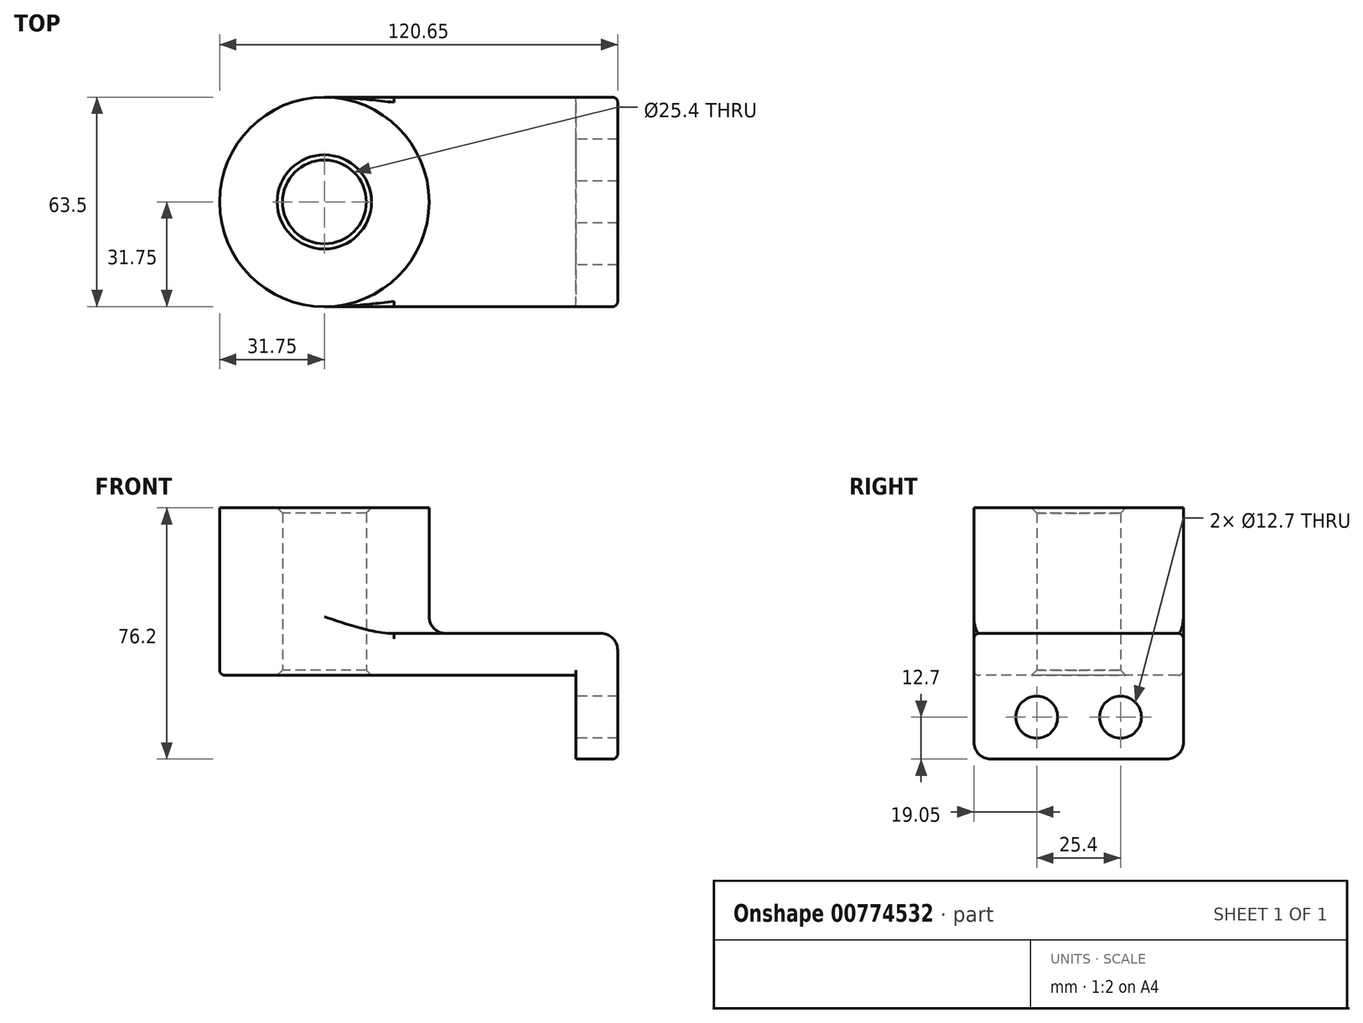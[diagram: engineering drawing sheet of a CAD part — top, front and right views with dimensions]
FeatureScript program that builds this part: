
annotation { "Feature Type Name" : "Feature", "Feature Type Description" : "" }
export const myFeature = defineFeature(function(context is Context, id is Id, definition is map)
    precondition{}
    {
        {
            var Q0;
            Q0=qCreatedBy(makeId("Top.planeOp"),FACE);
            var sketch = newSketch(context, id + "F0", { "sketchPlane" : qUnion([Q0])});
            skLineSegment(sketch, "E0.bottom", {"start": v(-38.1, 31.75) * mm, "end": v(38.1, 31.75) * mm});
            skLineSegment(sketch, "E0.top", {"start": v(-38.1, -31.75) * mm, "end": v(38.1, -31.75) * mm});
            skLineSegment(sketch, "E0.left", {"start": v(-38.1, 31.75) * mm, "end": v(-38.1, -31.75) * mm});
            skLineSegment(sketch, "E0.right", {"start": v(38.1, 31.75) * mm, "end": v(38.1, -31.75) * mm});
            skPoint(sketch, "E0.middle", {"position": v(0, 0) * mm});
            skCircle(sketch, "E1", {"center": v(-38.1, 0) * mm, "radius": 31.75 * mm});
            skCircle(sketch, "E2", {"center": v(-38.1, 0) * mm, "radius": 12.7 * mm});
            skSolve(sketch);
        }
        {
            var Q0;
            Q0 = qSketchRegion(id + "F0", true);
            extrude(context, id + "F1", {"entities" : qUnion([Q0]), "depth" : 12.7 * mm, "offsetDistance" : 25.4 * mm});
        }
        {
            var Q0;
            {var subQ1=sQuery(id+"F0.wireOp",EDGE,"E0.left");var subQ3=sQuery(id+"F0.wireOp",EDGE,"E2");var subQ4=makeQuery(id+"F0.imprint","INTERSECT",VERTEX,{"disambiguationData":[OD(0.0)],"derivedFrom":[subQ1,subQ3]});Q0=makeQuery(id+"F0.imprint","IMPRINT",FACE,{"disambiguationData":[TD([[makeQuery(id+"F0.imprint","IMPRINT",EDGE,{"disambiguationData":[TD([[subQ4,-1.0]])],"derivedFrom":subQ3}),-1.0]])]});}
            var Q1;
            {var subQ1=sQuery(id+"F0.wireOp",EDGE,"E0.left");var subQ3=sQuery(id+"F0.wireOp",EDGE,"E2");var subQ4=makeQuery(id+"F0.imprint","INTERSECT",VERTEX,{"disambiguationData":[OD(0.0)],"derivedFrom":[subQ1,subQ3]});Q1=makeQuery(id+"F0.imprint","IMPRINT",FACE,{"disambiguationData":[TD([[makeQuery(id+"F0.imprint","IMPRINT",EDGE,{"disambiguationData":[TD([[subQ4,1.0]])],"derivedFrom":subQ3}),-1.0]])]});}
            extrude(context, id + "F2", {"entities" : qUnion([Q0, Q1]), "operationType" : NewBodyOperationType.ADD, "depth" : 50.8 * mm, "offsetDistance" : 25.4 * mm});
        }
        {
            var Q0;
            Q0=makeQuery(id+"F1.opExtrude","SWEPT_FACE",FACE,{"disambiguationData":[OSD([sQuery(id+"F0.wireOp",EDGE,"E0.right")])]});
            var sketch = newSketch(context, id + "F3", { "sketchPlane" : qUnion([Q0])});
            skLineSegment(sketch, "E3.bottom", {"start": v(-31.75, 12.7) * mm, "end": v(31.75, 12.7) * mm});
            skLineSegment(sketch, "E3.top", {"start": v(-31.75, -25.4) * mm, "end": v(31.75, -25.4) * mm});
            skLineSegment(sketch, "E3.left", {"start": v(-31.75, 12.7) * mm, "end": v(-31.75, -25.4) * mm});
            skLineSegment(sketch, "E3.right", {"start": v(31.75, 12.7) * mm, "end": v(31.75, -25.4) * mm});
            skCircle(sketch, "E4", {"center": v(-12.7, -12.7) * mm, "radius": 6.35 * mm});
            skLineSegment(sketch, "E5", {"start": v(0, 0) * mm, "end": v(0, -25.4) * mm, "construction": true});
            skCircle(sketch, "E6.MirrorC", {"center": v(12.7, -12.7) * mm, "radius": 6.35 * mm});
            skSolve(sketch);
        }
        {
            var Q0;
            {var subQ0=sQuery(id+"F3.wireOp",EDGE,"E3.bottom");Q0=makeQuery(id+"F3.imprint","IMPRINT",FACE,{"disambiguationData":[TD([[makeQuery(id+"F3.imprint","IMPRINT",EDGE,{"derivedFrom":subQ0}),1.0]])]});}
            var Q1;
            {var subQ2=sQuery(id+"F3.wireOp",EDGE,"E3.top");Q1=makeQuery(id+"F3.imprint","IMPRINT",FACE,{"disambiguationData":[TD([[makeQuery(id+"F3.imprint","IMPRINT",EDGE,{"derivedFrom":subQ2}),1.0]])]});}
            extrude(context, id + "F4", {"entities" : qUnion([Q0, Q1]), "operationType" : NewBodyOperationType.ADD, "depth" : 12.7 * mm, "offsetDistance" : 25.4 * mm});
        }
        {
            var Q0;
            {var subQ0=sQuery(id+"F0.wireOp",EDGE,"E1");Q0=makeQuery(id+"F2.boolean.opBoolean","INTERSECT",EDGE,{"derivedFrom":[makeQuery(id+"F1.opExtrude","CAP_FACE",FACE,{"disambiguationData":[OSD([sQuery(id+"F0.wireOp",EDGE,"E0.bottom"),sQuery(id+"F0.wireOp",EDGE,"E0.top"),sQuery(id+"F0.wireOp",EDGE,"E0.right"),subQ0,sQuery(id+"F0.wireOp",EDGE,"E2")])],"isStart":false}),makeQuery(id+"F2.opExtrude","SWEPT_FACE",FACE,{"disambiguationData":[OSD([subQ0])]})]});}
            var Q1;
            Q1=makeQuery(id+"F4.opExtrude","CAP_EDGE",EDGE,{"disambiguationData":[OSD([sQuery(id+"F3.wireOp",EDGE,"E3.bottom")])],"isStart":false});
            var Q2;
            Q2=makeQuery(id+"F4.opExtrude","SWEPT_EDGE",EDGE,{"disambiguationData":[OSD([sQuery(id+"F3.wireOp",EDGE,"E3.top"),sQuery(id+"F3.wireOp",EDGE,"E3.left")])]});
            var Q3;
            Q3=makeQuery(id+"F4.opExtrude","SWEPT_EDGE",EDGE,{"disambiguationData":[OSD([sQuery(id+"F3.wireOp",EDGE,"E3.top"),sQuery(id+"F3.wireOp",EDGE,"E3.right")])]});
            fillet(context, id + "F5", {"entities" : qUnion([Q0, Q1, Q2, Q3]), "radius" : 5.08 * mm, "tangentPropagation" : true, "allowEdgeOverflow" : false});
        }
        {
            var Q0;
            Q0=makeQuery(id+"F4.boolean.opBoolean","MERGE",EDGE,{"derivedFrom":[makeQuery(id+"F1.opExtrude","CAP_EDGE",EDGE,{"disambiguationData":[OSD([sQuery(id+"F0.wireOp",EDGE,"E0.top")])],"isStart":false}),makeQuery(id+"F4.opExtrude","SWEPT_EDGE",EDGE,{"disambiguationData":[OSD([sQuery(id+"F3.wireOp",EDGE,"E3.bottom"),sQuery(id+"F3.wireOp",EDGE,"E3.left")])]})]});
            var Q1;
            Q1=makeQuery(id+"F1.opExtrude","CAP_EDGE",EDGE,{"disambiguationData":[OSD([sQuery(id+"F0.wireOp",EDGE,"E0.top")])],"isStart":true});
            var Q2;
            Q2=makeQuery(id+"F1.opExtrude","CAP_EDGE",EDGE,{"disambiguationData":[OSD([sQuery(id+"F0.wireOp",EDGE,"E0.right")])],"isStart":true});
            fillet(context, id + "F6", {"entities" : qUnion([Q0, Q1, Q2]), "radius" : 1.59 * mm, "tangentPropagation" : true, "allowEdgeOverflow" : false});
        }
        {
            var Q0;
            {var subQ0=sQuery(id+"F0.wireOp",EDGE,"E2");Q0=makeQuery(id+"F2.boolean.opBoolean","MERGE",FACE,{"derivedFrom":[makeQuery(id+"F1.opExtrude","SWEPT_FACE",FACE,{"disambiguationData":[OSD([subQ0])]}),makeQuery(id+"F2.opExtrude","SWEPT_FACE",FACE,{"disambiguationData":[OSD([subQ0])]})]});}
            chamfer(context, id + "F7", {"entities" : qUnion([Q0]), "width" : 1.59 * mm, "tangentPropagation" : true});
        }
    });
